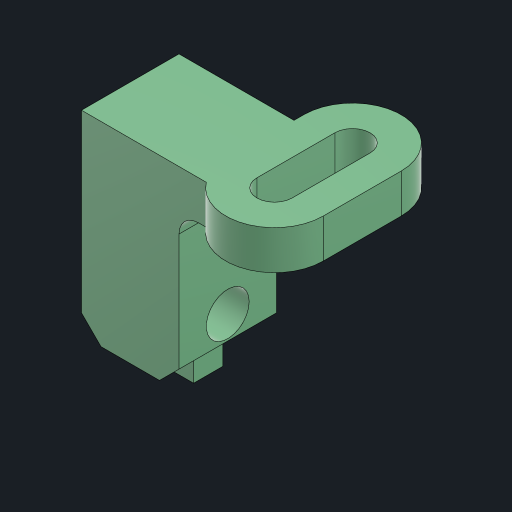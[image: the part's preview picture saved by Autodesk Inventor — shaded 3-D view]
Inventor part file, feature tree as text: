
AUTODESK INVENTOR PART (.ipt)
format: ipt  version: 2023 (Build 270158000, 158)  size: 191,488 bytes
history: native  units: mm
features: sketch x3, extrude x3, other x2, hole x1, fillet x1, chamfer x1
ambient origin geometry x8: Origin, YZ Plane, XZ Plane, XY Plane, X Axis, Y Axis, Z Axis, Center Point
bodies: Body1 (feature_tree)
feature tree (11):
  other  "ソリッド1"
  sketch  "スケッチ1"
  extrude  "押し出し1"  Depth=1.8mm
  extrude  "押し出し4"  Depth=4.0mm
  hole  "穴2"  [1 undecoded]
  fillet  "フィレット2"  Radius=2.0mm
  other  "作業平面2"
  chamfer  "面取り1"  Distance=5.0mm
  extrude  "押し出し5"  Depth=5.9mm
  sketch  "スケッチ5"
  sketch  "スケッチ6"
note: 1 required parameter value undecoded (feature->parameter linkage not recoverable at this tier; creation-order binding heuristic only, values carry confidence <= 0.55)
